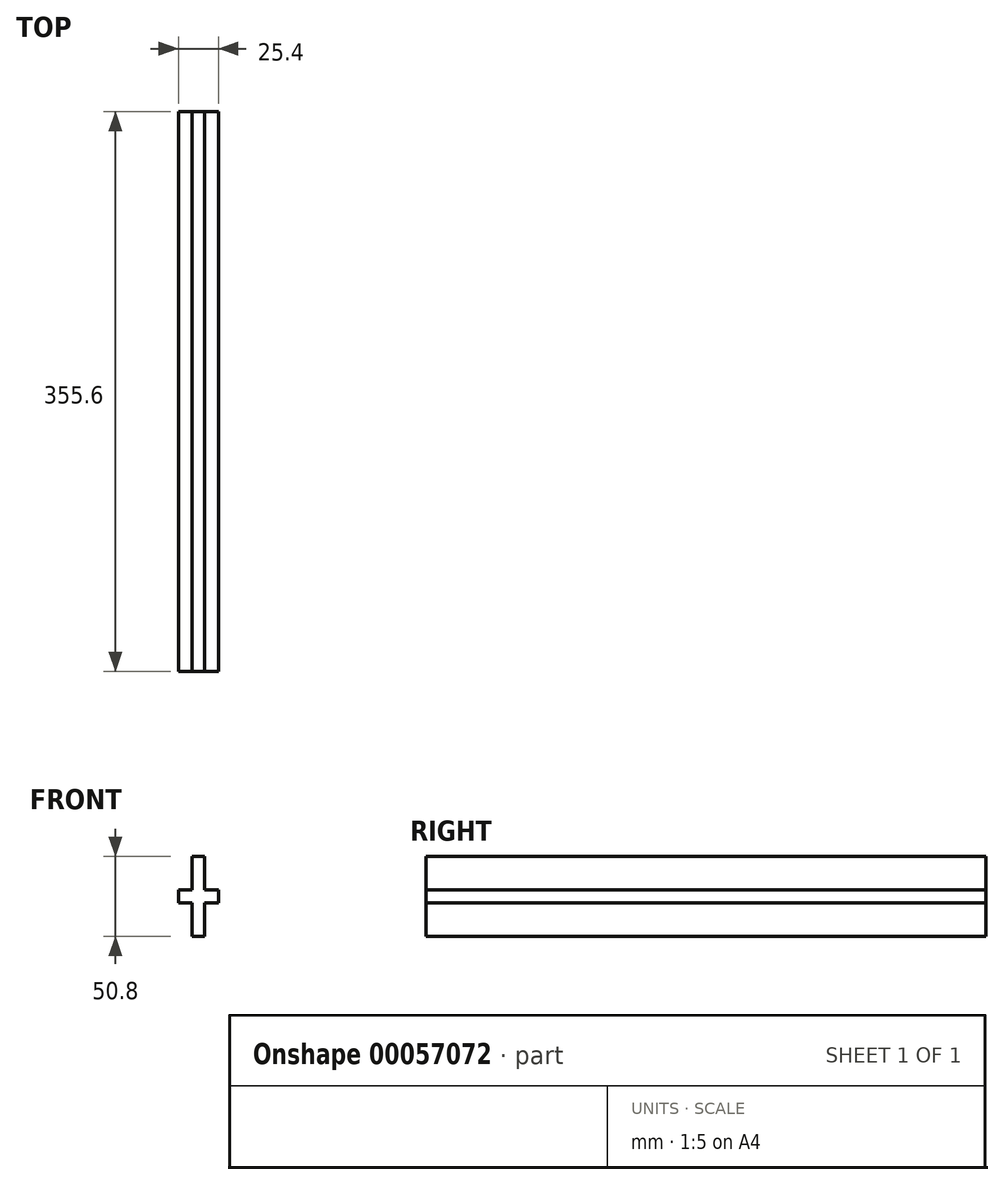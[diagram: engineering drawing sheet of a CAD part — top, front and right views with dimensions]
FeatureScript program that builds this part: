
annotation { "Feature Type Name" : "Feature", "Feature Type Description" : "" }
export const myFeature = defineFeature(function(context is Context, id is Id, definition is map)
    precondition{}
    {
        {
            var Q0;
            Q0=qCreatedBy(makeId("Front.planeOp"),FACE);
            var sketch = newSketch(context, id + "F0", { "sketchPlane" : qUnion([Q0])});
            skLineSegment(sketch, "E0.rect.bottom", {"start": v(-3.87, 25.4) * mm, "end": v(3.87, 25.4) * mm});
            skLineSegment(sketch, "E0.rect.top", {"start": v(-3.87, -25.4) * mm, "end": v(3.87, -25.4) * mm});
            skLineSegment(sketch, "E0.rect.left", {"start": v(-3.87, 25.4) * mm, "end": v(-3.87, -25.4) * mm});
            skLineSegment(sketch, "E0.rect.right", {"start": v(3.87, 25.4) * mm, "end": v(3.87, -25.4) * mm});
            skPoint(sketch, "E0.rect.middle", {"position": v(0, 0) * mm});
            skLineSegment(sketch, "E1.rect.bottom", {"start": v(-12.7, -4.09) * mm, "end": v(12.7, -4.09) * mm});
            skLineSegment(sketch, "E1.rect.top", {"start": v(-12.7, 4.09) * mm, "end": v(12.7, 4.09) * mm});
            skLineSegment(sketch, "E1.rect.left", {"start": v(-12.7, -4.09) * mm, "end": v(-12.7, 4.09) * mm});
            skLineSegment(sketch, "E1.rect.right", {"start": v(12.7, -4.09) * mm, "end": v(12.7, 4.09) * mm});
            skSolve(sketch);
        }
        {
            var Q0;
            {var subQ0=sQuery(id+"F0.wireOp",EDGE,"E0.rect.bottom");Q0=makeQuery(id+"F0.imprint","IMPRINT",FACE,{"disambiguationData":[TD([[makeQuery(id+"F0.imprint","IMPRINT",EDGE,{"derivedFrom":subQ0}),-1.0]])]});}
            var Q1;
            {var subQ5=sQuery(id+"F0.wireOp",EDGE,"E1.rect.left");Q1=makeQuery(id+"F0.imprint","IMPRINT",FACE,{"disambiguationData":[TD([[makeQuery(id+"F0.imprint","IMPRINT",EDGE,{"derivedFrom":subQ5}),-1.0]])]});}
            var Q2;
            {var subQ5=sQuery(id+"F0.wireOp",EDGE,"E1.rect.right");Q2=makeQuery(id+"F0.imprint","IMPRINT",FACE,{"disambiguationData":[TD([[makeQuery(id+"F0.imprint","IMPRINT",EDGE,{"derivedFrom":subQ5}),1.0]])]});}
            var Q3;
            {var subQ0=sQuery(id+"F0.wireOp",EDGE,"E0.rect.top");Q3=makeQuery(id+"F0.imprint","IMPRINT",FACE,{"disambiguationData":[TD([[makeQuery(id+"F0.imprint","IMPRINT",EDGE,{"derivedFrom":subQ0}),1.0]])]});}
            var Q4;
            {var subQ0=sQuery(id+"F0.wireOp",EDGE,"E1.rect.top");var subQ1=sQuery(id+"F0.wireOp",EDGE,"E0.rect.left");var subQ2=makeQuery(id+"F0.imprint","INTERSECT",VERTEX,{"derivedFrom":[subQ1,subQ0]});Q4=makeQuery(id+"F0.imprint","IMPRINT",FACE,{"disambiguationData":[TD([[makeQuery(id+"F0.imprint","IMPRINT",EDGE,{"disambiguationData":[TD([[subQ2,-1.0]])],"derivedFrom":subQ1}),1.0]])]});}
            extrude(context, id + "F1", {"entities" : qUnion([Q0, Q1, Q2, Q3, Q4]), "depth" : 355.6 * mm});
        }
    });
